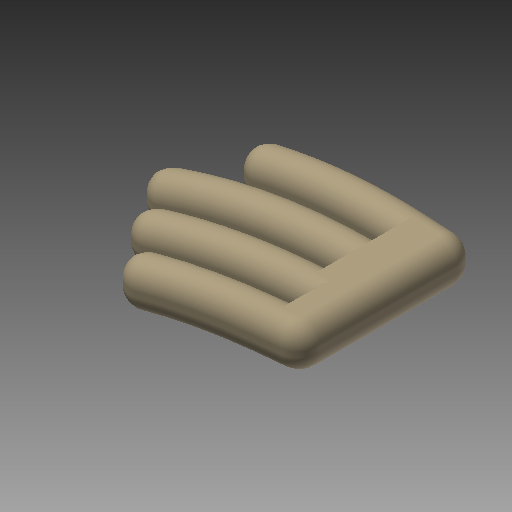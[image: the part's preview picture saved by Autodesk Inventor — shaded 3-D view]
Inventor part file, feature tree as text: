
AUTODESK INVENTOR PART (.ipt)
format: ipt  version: 2022 (Build 260153000, 153)  size: 641,536 bytes
history: native  units: mm (DEFAULTED — no unit token found)
features: fillet x3, other x2, extrude x2, sketch x2, projected_geometry x2, plane x1
ambient origin geometry x8: Origin, YZ Plane, XZ Plane, XY Plane, X Axis, Y Axis, Z Axis, Center Point
bodies: Solid1 (feature_tree)
feature tree (12):
  other  "iMan - 2D BODY"
  extrude  "Extrusion1"  Depth=10.0mm
  extrude  "Extrusion2"  Depth=1.9304mm
  fillet  "Fillet1"  Radius=96.52mm
  fillet  "Fillet3"  Radius=57.912mm
  fillet  "Fillet4"  Radius=96.52mm
  other  "Work Axis1"
  plane  "Work Plane1"
  sketch  "Sketch1"  dims[d1=10.0mm d16=0.523599mm]
  sketch  "Sketch2"  dims[d17=0.523599mm d18=3.490659mm d19=96.52mm d20=57.912mm d22=96.52mm d23=4.826mm d24=38.608mm d25=0.0mm d26=9.652mm d28=19.304mm d29=0.0mm d30=8.4455mm d31=1.9304mm d32=91.95016mm d33=80.45639mm]
  projected_geometry  "Projected Loop1"
  projected_geometry  "Projected Loop2"
